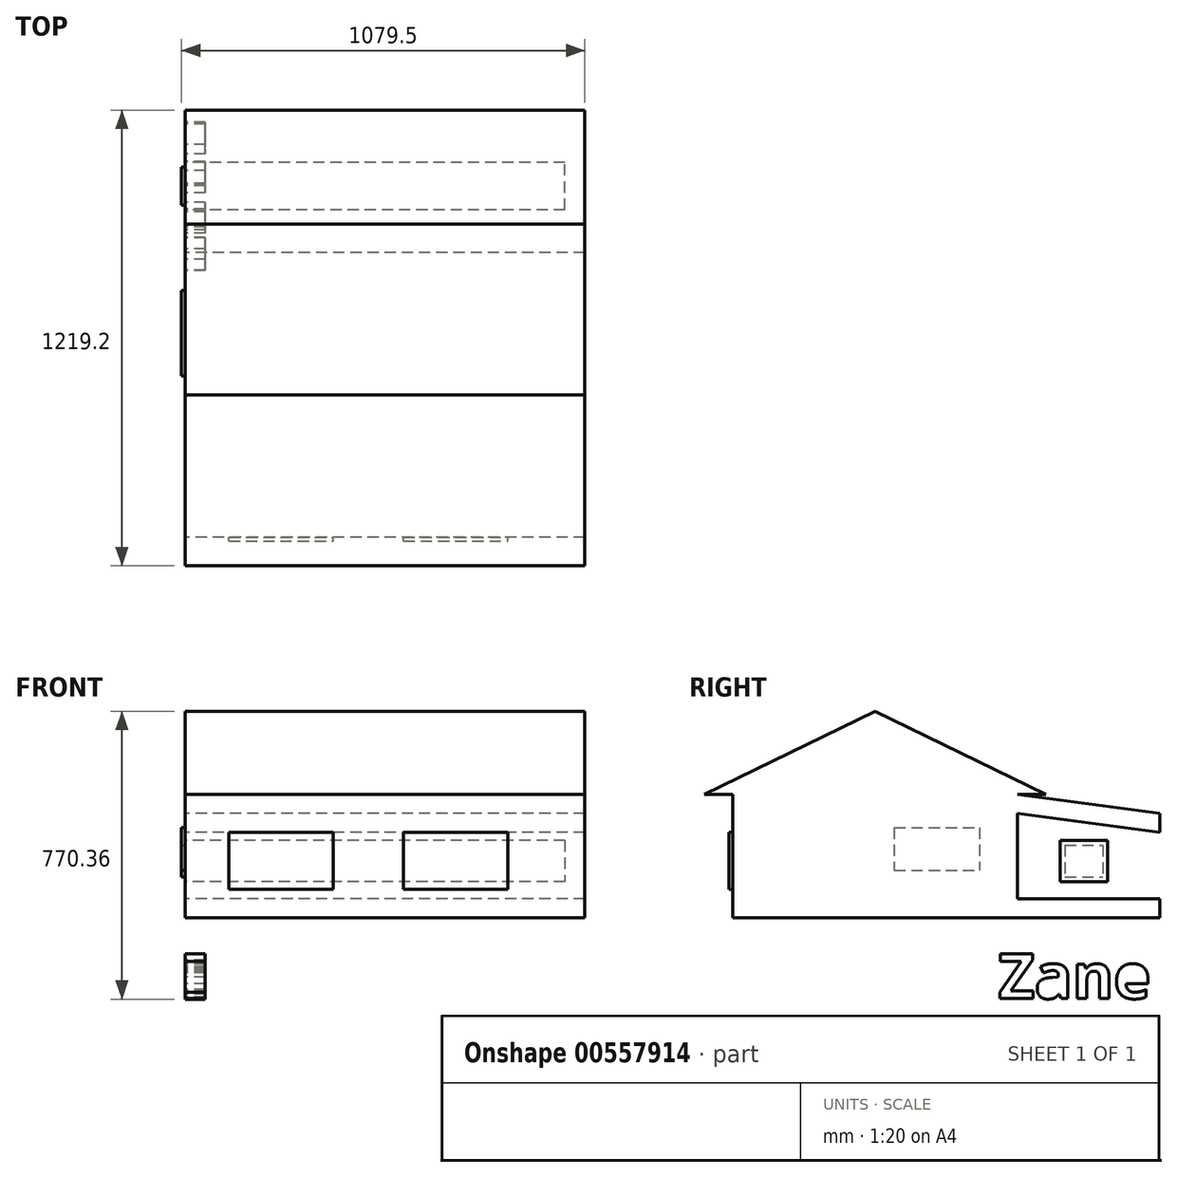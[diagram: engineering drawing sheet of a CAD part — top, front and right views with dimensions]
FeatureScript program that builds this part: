
annotation { "Feature Type Name" : "Feature", "Feature Type Description" : "" }
export const myFeature = defineFeature(function(context is Context, id is Id, definition is map)
    precondition{}
    {
        {
            var Q0;
            Q0=qCreatedBy(makeId("Right.planeOp"),FACE);
            var sketch = newSketch(context, id + "F0", { "sketchPlane" : qUnion([Q0])});
            skLineSegment(sketch, "E0", {"start": v(0, 0) * mm, "end": v(381, 0) * mm});
            skLineSegment(sketch, "E1", {"start": v(0, 0) * mm, "end": v(-381, 0) * mm});
            skLineSegment(sketch, "E2", {"start": v(0, 0) * mm, "end": v(0, 184.1) * mm});
            skLineSegment(sketch, "E3", {"start": v(0, 184.1) * mm, "end": v(-381, 0) * mm});
            skLineSegment(sketch, "E4", {"start": v(-381, 0) * mm, "end": v(-457.2, 0) * mm});
            skLineSegment(sketch, "E5", {"start": v(0, 184.1) * mm, "end": v(381, 0) * mm});
            skLineSegment(sketch, "E6", {"start": v(0, 184.1) * mm, "end": v(0, 222.2) * mm});
            skLineSegment(sketch, "E7", {"start": v(0, 222.2) * mm, "end": v(-457.2, 0) * mm});
            skLineSegment(sketch, "E8", {"start": v(381, 0) * mm, "end": v(457.2, 0) * mm});
            skLineSegment(sketch, "E9", {"start": v(457.2, 0) * mm, "end": v(0, 222.2) * mm});
            skLineSegment(sketch, "E10", {"start": v(-381, 0) * mm, "end": v(-381, -279.4) * mm});
            skLineSegment(sketch, "E11", {"start": v(381, 0) * mm, "end": v(381, -279.4) * mm});
            skLineSegment(sketch, "E12", {"start": v(-381, -279.4) * mm, "end": v(381, -279.4) * mm});
            skLineSegment(sketch, "E13", {"start": v(-381, -279.4) * mm, "end": v(-381, -330.2) * mm});
            skLineSegment(sketch, "E14", {"start": v(381, -279.4) * mm, "end": v(381, -330.2) * mm});
            skLineSegment(sketch, "E15", {"start": v(381, -330.2) * mm, "end": v(-381, -330.2) * mm});
            skLineSegment(sketch, "E16", {"start": v(381, -279.4) * mm, "end": v(762, -279.4) * mm});
            skLineSegment(sketch, "E17", {"start": v(381, -330.2) * mm, "end": v(762, -330.2) * mm});
            skLineSegment(sketch, "E18", {"start": v(762, -279.4) * mm, "end": v(762, -50.8) * mm});
            skLineSegment(sketch, "E19", {"start": v(762, -50.8) * mm, "end": v(381, 0) * mm});
            skLineSegment(sketch, "E20", {"start": v(762, -279.4) * mm, "end": v(762, -330.2) * mm});
            skLineSegment(sketch, "E21", {"start": v(381, 0) * mm, "end": v(381, -34.9) * mm});
            skLineSegment(sketch, "E22", {"start": v(381, 0) * mm, "end": v(381, -50.8) * mm});
            skLineSegment(sketch, "E23", {"start": v(762, -50.8) * mm, "end": v(762, -101.6) * mm});
            skLineSegment(sketch, "E24", {"start": v(381, -50.8) * mm, "end": v(762, -101.6) * mm});
            skLineSegment(sketch, "E25.bottom", {"start": v(508, -136.25) * mm, "end": v(609.6, -136.25) * mm});
            skLineSegment(sketch, "E25.top", {"start": v(508, -220.66) * mm, "end": v(609.6, -220.66) * mm});
            skLineSegment(sketch, "E25.left", {"start": v(508, -136.25) * mm, "end": v(508, -220.66) * mm});
            skLineSegment(sketch, "E25.right", {"start": v(609.6, -136.25) * mm, "end": v(609.6, -220.66) * mm});
            skLineSegment(sketch, "E26.0", {"start": v(495.3, -233.36) * mm, "end": v(622.3, -233.36) * mm});
            skLineSegment(sketch, "E26.1", {"start": v(495.3, -123.55) * mm, "end": v(495.3, -233.36) * mm});
            skLineSegment(sketch, "E26.2", {"start": v(495.3, -123.55) * mm, "end": v(622.3, -123.55) * mm});
            skLineSegment(sketch, "E26.3", {"start": v(622.3, -123.55) * mm, "end": v(622.3, -233.36) * mm});
            skLineSegment(sketch, "E27", {"start": v(-279.4, -279.4) * mm, "end": v(-279.4, -101.6) * mm});
            skLineSegment(sketch, "E28", {"start": v(-279.4, -101.6) * mm, "end": v(-203.2, -101.6) * mm});
            skLineSegment(sketch, "E29", {"start": v(-203.2, -101.6) * mm, "end": v(-203.2, -279.4) * mm});
            skLineSegment(sketch, "E30.bottom", {"start": v(50.8, -88.9) * mm, "end": v(279.4, -88.9) * mm});
            skLineSegment(sketch, "E30.top", {"start": v(50.8, -203.2) * mm, "end": v(279.4, -203.2) * mm});
            skLineSegment(sketch, "E30.left", {"start": v(50.8, -88.9) * mm, "end": v(50.8, -203.2) * mm});
            skLineSegment(sketch, "E30.right", {"start": v(279.4, -88.9) * mm, "end": v(279.4, -203.2) * mm});
            skLineSegment(sketch, "E31.0", {"start": v(-177.8, -76.2) * mm, "end": v(-177.8, -279.4) * mm});
            skLineSegment(sketch, "E31.1", {"start": v(-304.8, -76.2) * mm, "end": v(-177.8, -76.2) * mm});
            skLineSegment(sketch, "E31.2", {"start": v(-304.8, -279.4) * mm, "end": v(-304.8, -76.2) * mm});
            skLineSegment(sketch, "E32.0", {"start": v(38.1, -76.2) * mm, "end": v(292.1, -76.2) * mm});
            skLineSegment(sketch, "E32.1", {"start": v(38.1, -76.2) * mm, "end": v(38.1, -215.9) * mm});
            skLineSegment(sketch, "E32.2", {"start": v(38.1, -215.9) * mm, "end": v(292.1, -215.9) * mm});
            skLineSegment(sketch, "E32.3", {"start": v(292.1, -76.2) * mm, "end": v(292.1, -215.9) * mm});
            skText(sketch, "E33", { "text": "Zane", "fontName": "OpenSans-Bold.ttf"});
            const initialGuessF0  = {"E33": [0.32896, -0.54651, 1, 0, 0.1209]};
            skSetInitialGuess(sketch, initialGuessF0);
            skSolve(sketch);
        }
        {
            var Q0;
            {var subQ5=sQuery(id+"F0.wireOp",EDGE,"E13");Q0=makeQuery(id+"F0.imprint","IMPRINT",FACE,{"disambiguationData":[TD([[makeQuery(id+"F0.imprint","IMPRINT",EDGE,{"derivedFrom":subQ5}),1.0]])]});}
            var Q1;
            {var subQ3=sQuery(id+"F0.wireOp",EDGE,"E0");Q1=makeQuery(id+"F0.imprint","IMPRINT",FACE,{"disambiguationData":[TD([[makeQuery(id+"F0.imprint","IMPRINT",EDGE,{"derivedFrom":subQ3}),-1.0]])]});}
            var Q2;
            Q2=makeQuery(id+"F0.imprint","IMPRINT",FACE,{"disambiguationData":[TD([[makeQuery(id+"F0.imprint","IMPRINT",EDGE,{"derivedFrom":sQuery(id+"F0.wireOp",EDGE,"E11")}),1.0]])]});
            var Q3;
            Q3=makeQuery(id+"F0.imprint","IMPRINT",FACE,{"disambiguationData":[TD([[makeQuery(id+"F0.imprint","IMPRINT",EDGE,{"derivedFrom":sQuery(id+"F0.wireOp",EDGE,"E0")}),1.0]])]});
            var Q4;
            Q4=makeQuery(id+"F0.imprint","IMPRINT",FACE,{"disambiguationData":[TD([[makeQuery(id+"F0.imprint","IMPRINT",EDGE,{"derivedFrom":sQuery(id+"F0.wireOp",EDGE,"E1")}),-1.0]])]});
            var Q5;
            Q5=makeQuery(id+"F0.imprint","IMPRINT",FACE,{"disambiguationData":[TD([[makeQuery(id+"F0.imprint","IMPRINT",EDGE,{"derivedFrom":sQuery(id+"F0.wireOp",EDGE,"eb17bb15-a73d-4942-90b0-c9872d0c6eb2.sketch_text.stroke-0")}),-1.0]])]});
            var Q6;
            Q6=makeQuery(id+"F0.imprint","IMPRINT",FACE,{"disambiguationData":[TD([[makeQuery(id+"F0.imprint","IMPRINT",EDGE,{"derivedFrom":sQuery(id+"F0.wireOp",EDGE,"E30.bottom")}),-1.0]])]});
            var Q7;
            Q7=makeQuery(id+"F0.imprint","IMPRINT",FACE,{"disambiguationData":[TD([[makeQuery(id+"F0.imprint","IMPRINT",EDGE,{"derivedFrom":sQuery(id+"F0.wireOp",EDGE,"eb17bb15-a73d-4942-90b0-c9872d0c6eb2.sketch_text.stroke-52")}),1.0]])]});
            var Q8;
            Q8=makeQuery(id+"F0.imprint","IMPRINT",FACE,{"disambiguationData":[TD([[makeQuery(id+"F0.imprint","IMPRINT",EDGE,{"derivedFrom":sQuery(id+"F0.wireOp",EDGE,"eb17bb15-a73d-4942-90b0-c9872d0c6eb2.sketch_text.stroke-52")}),-1.0]])]});
            var Q9;
            Q9=makeQuery(id+"F0.imprint","IMPRINT",FACE,{"disambiguationData":[TD([[makeQuery(id+"F0.imprint","IMPRINT",EDGE,{"derivedFrom":sQuery(id+"F0.wireOp",EDGE,"E3")}),-1.0]])]});
            var Q10;
            Q10=makeQuery(id+"F0.imprint","IMPRINT",FACE,{"disambiguationData":[TD([[makeQuery(id+"F0.imprint","IMPRINT",EDGE,{"derivedFrom":sQuery(id+"F0.wireOp",EDGE,"E5")}),1.0]])]});
            var Q11;
            Q11=makeQuery(id+"F0.imprint","IMPRINT",FACE,{"disambiguationData":[TD([[makeQuery(id+"F0.imprint","IMPRINT",EDGE,{"derivedFrom":sQuery(id+"F0.wireOp",EDGE,"E14")}),1.0]])]});
            var Q12;
            {var subQ3=sQuery(id+"F0.wireOp",EDGE,"E19");Q12=makeQuery(id+"F0.imprint","IMPRINT",FACE,{"disambiguationData":[TD([[makeQuery(id+"F0.imprint","IMPRINT",EDGE,{"derivedFrom":subQ3}),1.0]])]});}
            var Q13;
            Q13=makeQuery(id+"F0.imprint","IMPRINT",FACE,{"disambiguationData":[TD([[makeQuery(id+"F0.imprint","IMPRINT",EDGE,{"derivedFrom":sQuery(id+"F0.wireOp",EDGE,"eb17bb15-a73d-4942-90b0-c9872d0c6eb2.sketch_text.stroke-35")}),-1.0]])]});
            var Q14;
            Q14=makeQuery(id+"F0.imprint","IMPRINT",FACE,{"disambiguationData":[TD([[makeQuery(id+"F0.imprint","IMPRINT",EDGE,{"derivedFrom":sQuery(id+"F0.wireOp",EDGE,"E25.bottom")}),-1.0]])]});
            var Q15;
            Q15=makeQuery(id+"F0.imprint","IMPRINT",FACE,{"disambiguationData":[TD([[makeQuery(id+"F0.imprint","IMPRINT",EDGE,{"derivedFrom":sQuery(id+"F0.wireOp",EDGE,"eb17bb15-a73d-4942-90b0-c9872d0c6eb2.sketch_text.stroke-10")}),-1.0]])]});
            var Q16;
            Q16=makeQuery(id+"F0.imprint","IMPRINT",FACE,{"disambiguationData":[TD([[makeQuery(id+"F0.imprint","IMPRINT",EDGE,{"derivedFrom":sQuery(id+"F0.wireOp",EDGE,"eb17bb15-a73d-4942-90b0-c9872d0c6eb2.sketch_text.stroke-28")}),1.0]])]});
            var Q17;
            {var subQ0=sQuery(id+"F0.wireOp",EDGE,"E27");Q17=makeQuery(id+"F0.imprint","IMPRINT",FACE,{"disambiguationData":[TD([[makeQuery(id+"F0.imprint","IMPRINT",EDGE,{"derivedFrom":subQ0}),-1.0]])]});}
            var Q18;
            {var subQ0=sQuery(id+"F0.wireOp",EDGE,"E27");Q18=makeQuery(id+"F0.imprint","IMPRINT",FACE,{"disambiguationData":[TD([[makeQuery(id+"F0.imprint","IMPRINT",EDGE,{"derivedFrom":subQ0}),1.0]])]});}
            var Q19;
            Q19=makeQuery(id+"F0.imprint","IMPRINT",FACE,{"disambiguationData":[TD([[makeQuery(id+"F0.imprint","IMPRINT",EDGE,{"derivedFrom":sQuery(id+"F0.wireOp",EDGE,"E25.bottom")}),1.0]])]});
            var Q20;
            Q20=makeQuery(id+"F0.imprint","IMPRINT",FACE,{"disambiguationData":[TD([[makeQuery(id+"F0.imprint","IMPRINT",EDGE,{"derivedFrom":sQuery(id+"F0.wireOp",EDGE,"E30.bottom")}),1.0]])]});
            extrude(context, id + "F1", {"entities" : qUnion([Q0, Q1, Q2, Q3, Q4, Q5, Q6, Q7, Q8, Q9, Q10, Q11, Q12, Q13, Q14, Q15, Q16, Q17, Q18, Q19, Q20]), "depth" : 1016 * mm, "offsetDistance" : 25.4 * mm});
        }
        {
            var Q0;
            Q0=makeQuery(id+"F1.opExtrude","SWEPT_FACE",FACE,{"disambiguationData":[OSD([sQuery(id+"F0.wireOp",EDGE,"E10"),sQuery(id+"F0.wireOp",EDGE,"E13")])]});
            var sketch = newSketch(context, id + "F2", { "sketchPlane" : qUnion([Q0])});
            skLineSegment(sketch, "E34.bottom", {"start": v(116.4, -101.6) * mm, "end": v(395.8, -101.6) * mm});
            skLineSegment(sketch, "E34.top", {"start": v(116.4, -254) * mm, "end": v(395.8, -254) * mm});
            skLineSegment(sketch, "E34.left", {"start": v(116.4, -101.6) * mm, "end": v(116.4, -254) * mm});
            skLineSegment(sketch, "E34.right", {"start": v(395.8, -101.6) * mm, "end": v(395.8, -254) * mm});
            skLineSegment(sketch, "E35.bottom", {"start": v(584.2, -101.6) * mm, "end": v(863.6, -101.6) * mm});
            skLineSegment(sketch, "E35.top", {"start": v(584.2, -254) * mm, "end": v(863.6, -254) * mm});
            skLineSegment(sketch, "E35.left", {"start": v(584.2, -101.6) * mm, "end": v(584.2, -254) * mm});
            skLineSegment(sketch, "E35.right", {"start": v(863.6, -101.6) * mm, "end": v(863.6, -254) * mm});
            skSolve(sketch);
        }
        {
            var Q0;
            Q0=makeQuery(id+"F0.imprint","IMPRINT",FACE,{"disambiguationData":[TD([[makeQuery(id+"F0.imprint","IMPRINT",EDGE,{"derivedFrom":sQuery(id+"F0.wireOp",EDGE,"E33.sketch_text.stroke-35")}),-1.0]])]});
            var Q1;
            Q1=makeQuery(id+"F0.imprint","IMPRINT",FACE,{"disambiguationData":[TD([[makeQuery(id+"F0.imprint","IMPRINT",EDGE,{"derivedFrom":sQuery(id+"F0.wireOp",EDGE,"E33.sketch_text.stroke-0")}),-1.0]])]});
            var Q2;
            Q2=makeQuery(id+"F0.imprint","IMPRINT",FACE,{"disambiguationData":[TD([[makeQuery(id+"F0.imprint","IMPRINT",EDGE,{"derivedFrom":sQuery(id+"F0.wireOp",EDGE,"E33.sketch_text.stroke-28")}),1.0]])]});
            var Q3;
            Q3=makeQuery(id+"F0.imprint","IMPRINT",FACE,{"disambiguationData":[TD([[makeQuery(id+"F0.imprint","IMPRINT",EDGE,{"derivedFrom":sQuery(id+"F0.wireOp",EDGE,"E33.sketch_text.stroke-52")}),-1.0]])]});
            var Q4;
            Q4=makeQuery(id+"F0.imprint","IMPRINT",FACE,{"disambiguationData":[TD([[makeQuery(id+"F0.imprint","IMPRINT",EDGE,{"derivedFrom":sQuery(id+"F0.wireOp",EDGE,"E33.sketch_text.stroke-10")}),-1.0]])]});
            var Q5;
            Q5=makeQuery(id+"F0.imprint","IMPRINT",FACE,{"disambiguationData":[TD([[makeQuery(id+"F0.imprint","IMPRINT",EDGE,{"derivedFrom":sQuery(id+"F0.wireOp",EDGE,"E33.sketch_text.stroke-52")}),1.0]])]});
            var Q6;
            Q6=makeQuery(id+"F1.opExtrude","CAP_FACE",FACE,{"disambiguationData":[OSD([sQuery(id+"F0.wireOp",EDGE,"E4"),sQuery(id+"F0.wireOp",EDGE,"E7"),sQuery(id+"F0.wireOp",EDGE,"E8"),sQuery(id+"F0.wireOp",EDGE,"E9"),sQuery(id+"F0.wireOp",EDGE,"E10"),sQuery(id+"F0.wireOp",EDGE,"E13"),sQuery(id+"F0.wireOp",EDGE,"E15"),sQuery(id+"F0.wireOp",EDGE,"E17"),sQuery(id+"F0.wireOp",EDGE,"E18"),sQuery(id+"F0.wireOp",EDGE,"E19"),sQuery(id+"F0.wireOp",EDGE,"E20"),sQuery(id+"F0.wireOp",EDGE,"E23")])],"isStart":false});
            extrude(context, id + "F3", {"entities" : qUnion([Q0, Q1, Q2, Q3, Q4, Q5, Q6]), "operationType" : NewBodyOperationType.ADD, "depth" : 53.34 * mm, "offsetDistance" : 25.4 * mm});
        }
        {
            var Q0;
            {var subQ0=sQuery(id+"F0.wireOp",EDGE,"E27");Q0=makeQuery(id+"F0.imprint","IMPRINT",FACE,{"disambiguationData":[TD([[makeQuery(id+"F0.imprint","IMPRINT",EDGE,{"derivedFrom":subQ0}),-1.0]])]});}
            extrude(context, id + "F4", {"entities" : qUnion([Q0]), "operationType" : NewBodyOperationType.ADD, "depth" : 25.4 * mm, "offsetDistance" : 25.4 * mm});
        }
        {
            var Q0;
            Q0=makeQuery(id+"F2.imprint","IMPRINT",FACE,{"disambiguationData":[TD([[makeQuery(id+"F2.imprint","IMPRINT",EDGE,{"derivedFrom":sQuery(id+"F2.wireOp",EDGE,"E34.bottom")}),-1.0]])]});
            var Q1;
            Q1=makeQuery(id+"F2.imprint","IMPRINT",FACE,{"disambiguationData":[TD([[makeQuery(id+"F2.imprint","IMPRINT",EDGE,{"derivedFrom":sQuery(id+"F2.wireOp",EDGE,"E35.bottom")}),-1.0]])]});
            extrude(context, id + "F5", {"entities" : qUnion([Q0, Q1]), "operationType" : NewBodyOperationType.ADD, "depth" : 10.16 * mm, "offsetDistance" : 25.4 * mm});
        }
        {
            var Q0;
            Q0=makeQuery(id+"F0.imprint","IMPRINT",FACE,{"disambiguationData":[TD([[makeQuery(id+"F0.imprint","IMPRINT",EDGE,{"derivedFrom":sQuery(id+"F0.wireOp",EDGE,"E30.bottom")}),-1.0]])]});
            var Q1;
            Q1=makeQuery(id+"F0.imprint","IMPRINT",FACE,{"disambiguationData":[TD([[makeQuery(id+"F0.imprint","IMPRINT",EDGE,{"derivedFrom":sQuery(id+"F0.wireOp",EDGE,"E25.bottom")}),-1.0]])]});
            extrude(context, id + "F6", {"entities" : qUnion([Q0, Q1]), "operationType" : NewBodyOperationType.ADD, "oppositeDirection" : true, "depth" : 10.16 * mm, "offsetDistance" : 25.4 * mm});
        }
        {
            var Q0;
            {var subQ0=sQuery(id+"F0.wireOp",EDGE,"E27");Q0=makeQuery(id+"F0.imprint","IMPRINT",FACE,{"disambiguationData":[TD([[makeQuery(id+"F0.imprint","IMPRINT",EDGE,{"derivedFrom":subQ0}),-1.0]])]});}
            extrude(context, id + "F7", {"entities" : qUnion([Q0]), "operationType" : NewBodyOperationType.ADD, "depth" : 12.7 * mm, "offsetDistance" : 25.4 * mm});
        }
    });
